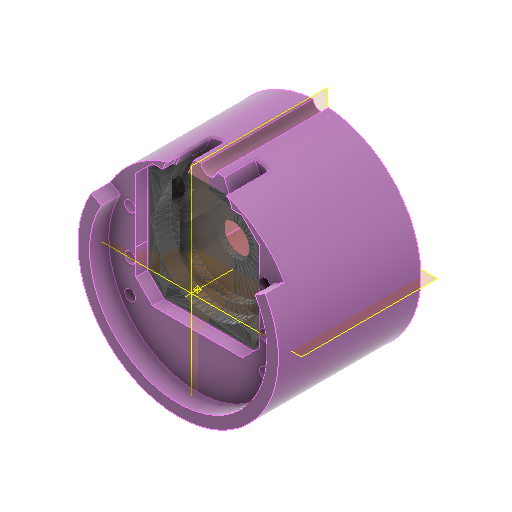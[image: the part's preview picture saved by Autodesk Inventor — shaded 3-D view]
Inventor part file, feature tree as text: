
AUTODESK INVENTOR PART (.ipt)
format: ipt  version: 2022.5 (Build 265521000, 521)  size: 443,904 bytes
history: native  units: mm
features: reference x20, other x7, extrude x6, sketch x4, plane x3, projected_geometry x3, hole x1
ambient origin geometry x8: Origin, YZ Plane, XZ Plane, XY Plane, X Axis, Y Axis, Z Axis, Center Point
bodies: Volumenkörper1 (feature_tree)
feature tree (44):
  extrude  "Extrusion1"  Depth=2.8mm
  sketch  "Skizze3"  dims[d0=2.8mm d1=2.8mm]
  plane  "Arbeitsebene1"
  extrude  "Extrusion2"  Depth=0.5mm
  extrude  "Extrusion3"  Depth=0.5mm
  hole  "Bohrung1"  [1 undecoded]
  extrude  "Extrusion5"  Depth=10.0mm TaperAngle=0.0deg
  other  "Arbeitspunkt1"
  plane  "Arbeitsebene2"
  plane  "Arbeitsebene3"
  extrude  "Extrusion6"  Depth=5.0mm
  extrude  "Extrusion7"  Depth=5.0mm TaperAngle=0.0deg
  reference  "Referenz1"
  reference  "Referenz2"
  reference  "Referenz3"
  reference  "Referenz4"
  reference  "Referenz5"
  reference  "Referenz7"
  reference  "Referenz8"
  reference  "Referenz9"
  reference  "Referenz10"
  reference  "Referenz11"
  reference  "Referenz12"
  reference  "Referenz13"
  reference  "Referenz14"
  reference  "Referenz15"
  reference  "Referenz16"
  reference  "Referenz17"
  reference  "Referenz18"
  reference  "Referenz19"
  sketch  "Skizze4"  dims[d2=8.0mm d3=0.0mm d4=0.5mm]
  projected_geometry  "Projizierte Kontur3"
  reference  "Referenz20"
  sketch  "Skizze7"  dims[d5=0.5mm d6=0.5mm]
  reference  "Referenz21"
  projected_geometry  "Projizierte Kontur5"
  other  "Arbeitsachse1"
  sketch  "Skizze8"  dims[d7=0.5mm d8=21.0mm d9=0.0mm d10=10.0mm d11=0.0mm d12=2.8mm d13=6.0mm d14=6.5mm d15=23.0mm d16=90.0deg d17=15.0mm d18=20.594885mm d22=0.5mm d23=3.0mm d24=0.0mm d25=46.0mm d26=5.0mm d27=0.0mm d28=4.0mm d29=0.0mm d30=0.0mm]
  projected_geometry  "Projizierte Kontur6"
  other  "MeshFeature1"
  other  "Planktoscope_Mini_Peristalticpump.iam"
  other  "00_Stepper_Motor_28BYJ-48:1"
  other  "Matchboxscope_bottom_v0:1"
  other  "Pump_Lid:1"
note: 1 required parameter value undecoded (feature->parameter linkage not recoverable at this tier; creation-order binding heuristic only, values carry confidence <= 0.55)
